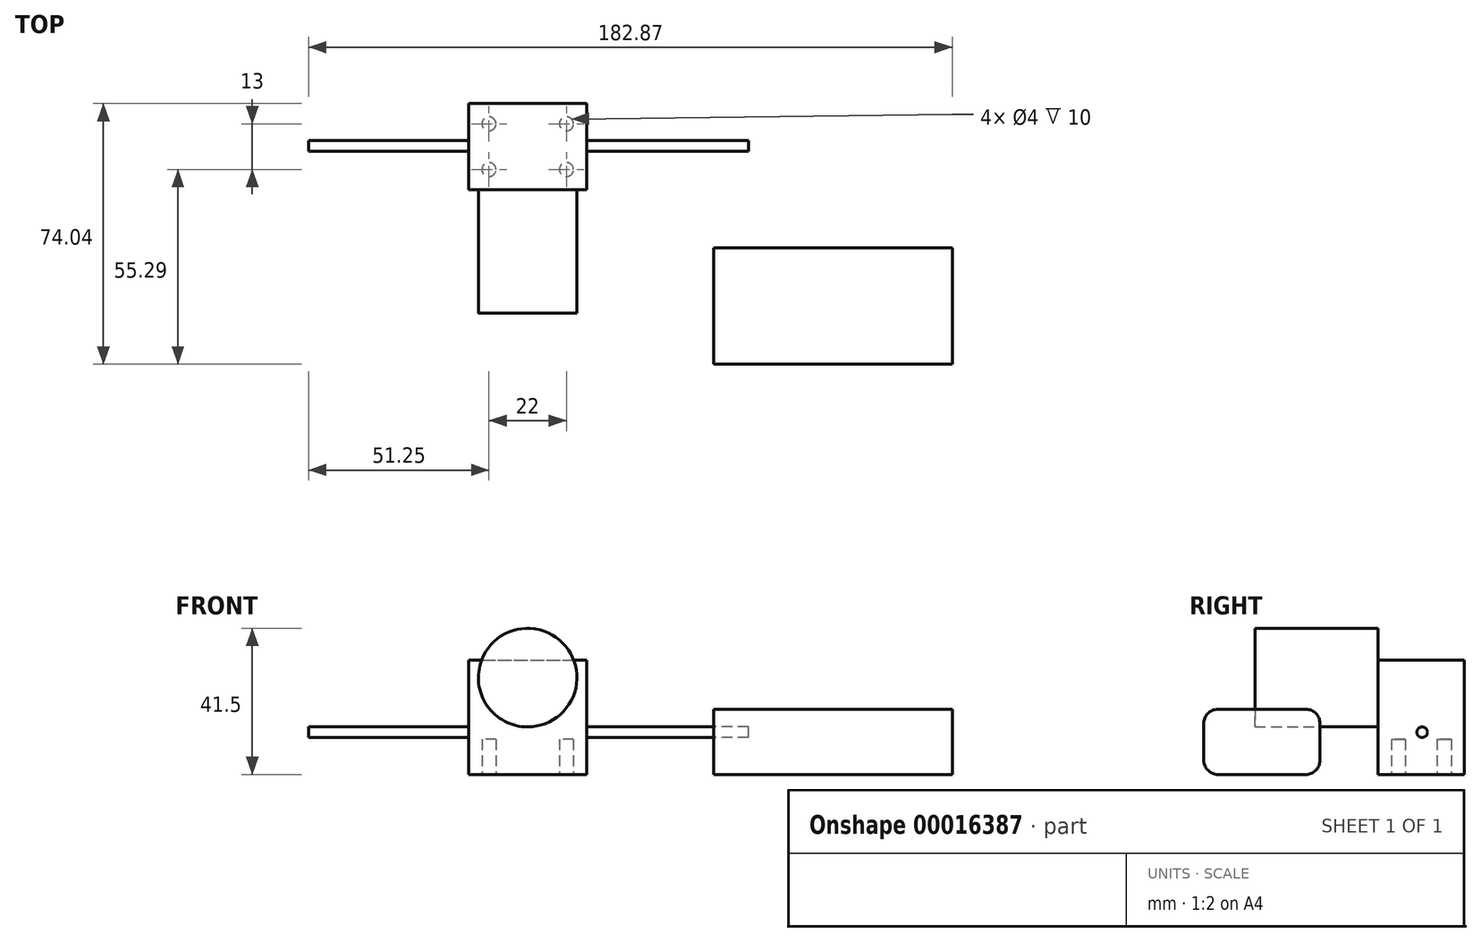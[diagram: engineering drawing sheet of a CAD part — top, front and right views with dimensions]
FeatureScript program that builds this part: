
annotation { "Feature Type Name" : "Feature", "Feature Type Description" : "" }
export const myFeature = defineFeature(function(context is Context, id is Id, definition is map)
    precondition{}
    {
        {
            var Q0;
            Q0=qCreatedBy(makeId("Top.planeOp"),FACE);
            var sketch = newSketch(context, id + "F0", { "sketchPlane" : qUnion([Q0])});
            skLineSegment(sketch, "E0.bottom", {"start": v(-16.75, 12.25) * mm, "end": v(16.75, 12.25) * mm});
            skLineSegment(sketch, "E0.top", {"start": v(-16.75, -12.25) * mm, "end": v(16.75, -12.25) * mm});
            skLineSegment(sketch, "E0.left", {"start": v(-16.75, 12.25) * mm, "end": v(-16.75, -12.25) * mm});
            skLineSegment(sketch, "E0.right", {"start": v(16.75, 12.25) * mm, "end": v(16.75, -12.25) * mm});
            skLineSegment(sketch, "E1.bottom", {"start": v(-11, 6.5) * mm, "end": v(11, 6.5) * mm, "construction": true});
            skLineSegment(sketch, "E1.top", {"start": v(-11, -6.5) * mm, "end": v(11, -6.5) * mm, "construction": true});
            skLineSegment(sketch, "E1.left", {"start": v(-11, 6.5) * mm, "end": v(-11, -6.5) * mm, "construction": true});
            skLineSegment(sketch, "E1.right", {"start": v(11, 6.5) * mm, "end": v(11, -6.5) * mm, "construction": true});
            skCircle(sketch, "E2", {"center": v(-11, 6.5) * mm, "radius": 2 * mm});
            skCircle(sketch, "E3", {"center": v(11, 6.5) * mm, "radius": 2 * mm});
            skCircle(sketch, "E4", {"center": v(11, -6.5) * mm, "radius": 2 * mm});
            skCircle(sketch, "E5", {"center": v(-11, -6.5) * mm, "radius": 2 * mm});
            skLineSegment(sketch, "E6", {"start": v(0, 0) * mm, "end": v(0, 25.06) * mm, "construction": true});
            skLineSegment(sketch, "E7", {"start": v(0, 0) * mm, "end": v(19.27, 0) * mm, "construction": true});
            skSolve(sketch);
        }
        {
            var Q0;
            Q0=makeQuery(id+"F0.imprint","IMPRINT",FACE,{"disambiguationData":[TD([[makeQuery(id+"F0.imprint","IMPRINT",EDGE,{"derivedFrom":sQuery(id+"F0.wireOp",EDGE,"E0.bottom")}),-1.0]])]});
            var Q1;
            Q1=makeQuery(id+"F0.imprint","IMPRINT",FACE,{"disambiguationData":[TD([[makeQuery(id+"F0.imprint","IMPRINT",EDGE,{"derivedFrom":sQuery(id+"F0.wireOp",EDGE,"E3")}),1.0]])]});
            var Q2;
            Q2=makeQuery(id+"F0.imprint","IMPRINT",FACE,{"disambiguationData":[TD([[makeQuery(id+"F0.imprint","IMPRINT",EDGE,{"derivedFrom":sQuery(id+"F0.wireOp",EDGE,"E2")}),1.0]])]});
            var Q3;
            Q3=makeQuery(id+"F0.imprint","IMPRINT",FACE,{"disambiguationData":[TD([[makeQuery(id+"F0.imprint","IMPRINT",EDGE,{"derivedFrom":sQuery(id+"F0.wireOp",EDGE,"E5")}),1.0]])]});
            var Q4;
            Q4=makeQuery(id+"F0.imprint","IMPRINT",FACE,{"disambiguationData":[TD([[makeQuery(id+"F0.imprint","IMPRINT",EDGE,{"derivedFrom":sQuery(id+"F0.wireOp",EDGE,"E4")}),1.0]])]});
            extrude(context, id + "F1", {"entities" : qUnion([Q0, Q1, Q2, Q3, Q4]), "depth" : 32.5 * mm});
        }
        {
            var Q0;
            Q0=makeQuery(id+"F1.opExtrude","SWEPT_FACE",FACE,{"disambiguationData":[OSD([sQuery(id+"F0.wireOp",EDGE,"E0.top")])]});
            var sketch = newSketch(context, id + "F2", { "sketchPlane" : qUnion([Q0])});
            skLineSegment(sketch, "E8", {"start": v(0, 0) * mm, "end": v(0, 55) * mm, "construction": true});
            skCircle(sketch, "E9", {"center": v(0, 27.5) * mm, "radius": 14 * mm});
            skSolve(sketch);
        }
        {
            var Q0;
            {var subQ0=makeQuery(id+"F1.opExtrude","CAP_EDGE",EDGE,{"disambiguationData":[OSD([sQuery(id+"F0.wireOp",EDGE,"E0.top")])],"isStart":false});var subQ1=sQuery(id+"F2.wireOp",EDGE,"E9");var subQ3=makeQuery(id+"F2.imprint","INTERSECT",VERTEX,{"disambiguationData":[OD(0.0)],"derivedFrom":[subQ0,subQ1]});Q0=makeQuery(id+"F2.imprint","IMPRINT",FACE,{"disambiguationData":[TD([[makeQuery(id+"F2.imprint","IMPRINT",EDGE,{"disambiguationData":[TD([[subQ3,-1.0]])],"derivedFrom":subQ1}),1.0]])]});}
            var Q1;
            {var subQ0=makeQuery(id+"F1.opExtrude","CAP_EDGE",EDGE,{"disambiguationData":[OSD([sQuery(id+"F0.wireOp",EDGE,"E0.top")])],"isStart":false});var subQ1=sQuery(id+"F2.wireOp",EDGE,"E9");var subQ3=makeQuery(id+"F2.imprint","INTERSECT",VERTEX,{"disambiguationData":[OD(0.0)],"derivedFrom":[subQ0,subQ1]});Q1=makeQuery(id+"F2.imprint","IMPRINT",FACE,{"disambiguationData":[TD([[makeQuery(id+"F2.imprint","IMPRINT",EDGE,{"disambiguationData":[TD([[subQ3,1.0]])],"derivedFrom":subQ1}),1.0]])]});}
            extrude(context, id + "F3", {"entities" : qUnion([Q0, Q1]), "operationType" : NewBodyOperationType.ADD, "depth" : 35 * mm});
        }
        {
            var Q0;
            Q0=makeQuery(id+"F0.imprint","IMPRINT",FACE,{"disambiguationData":[TD([[makeQuery(id+"F0.imprint","IMPRINT",EDGE,{"derivedFrom":sQuery(id+"F0.wireOp",EDGE,"E3")}),1.0]])]});
            var Q1;
            Q1=makeQuery(id+"F0.imprint","IMPRINT",FACE,{"disambiguationData":[TD([[makeQuery(id+"F0.imprint","IMPRINT",EDGE,{"derivedFrom":sQuery(id+"F0.wireOp",EDGE,"E2")}),1.0]])]});
            var Q2;
            Q2=makeQuery(id+"F0.imprint","IMPRINT",FACE,{"disambiguationData":[TD([[makeQuery(id+"F0.imprint","IMPRINT",EDGE,{"derivedFrom":sQuery(id+"F0.wireOp",EDGE,"E5")}),1.0]])]});
            var Q3;
            Q3=makeQuery(id+"F0.imprint","IMPRINT",FACE,{"disambiguationData":[TD([[makeQuery(id+"F0.imprint","IMPRINT",EDGE,{"derivedFrom":sQuery(id+"F0.wireOp",EDGE,"E4")}),1.0]])]});
            extrude(context, id + "F4", {"entities" : qUnion([Q0, Q1, Q2, Q3]), "operationType" : NewBodyOperationType.REMOVE, "depth" : 10 * mm});
        }
        {
            var Q0;
            Q0=makeQuery(id+"F1.opExtrude","SWEPT_FACE",FACE,{"disambiguationData":[OSD([sQuery(id+"F0.wireOp",EDGE,"E0.right")])]});
            var sketch = newSketch(context, id + "F5", { "sketchPlane" : qUnion([Q0])});
            skCircle(sketch, "E10", {"center": v(0.25, 12) * mm, "radius": 1.5 * mm});
            skSolve(sketch);
        }
        {
            var Q0;
            Q0=makeQuery(id+"F5.imprint","IMPRINT",FACE,{"disambiguationData":[TD([[makeQuery(id+"F5.imprint","IMPRINT",EDGE,{"derivedFrom":sQuery(id+"F5.wireOp",EDGE,"E10")}),1.0]])]});
            extrude(context, id + "F6", {"entities" : qUnion([Q0]), "operationType" : NewBodyOperationType.ADD, "depth" : 46 * mm, "hasSecondDirection" : true, "secondDirectionOppositeDirection" : true, "secondDirectionDepth" : 79 * mm});
        }
        {
            var Q0;
            Q0=qCreatedBy(makeId("Top.planeOp"),FACE);
            var sketch = newSketch(context, id + "F7", { "sketchPlane" : qUnion([Q0])});
            skLineSegment(sketch, "E11.bottom", {"start": v(52.82, -28.79) * mm, "end": v(120.62, -28.79) * mm});
            skLineSegment(sketch, "E11.top", {"start": v(52.82, -61.79) * mm, "end": v(120.62, -61.79) * mm});
            skLineSegment(sketch, "E11.left", {"start": v(52.82, -28.79) * mm, "end": v(52.82, -61.79) * mm});
            skLineSegment(sketch, "E11.right", {"start": v(120.62, -28.79) * mm, "end": v(120.62, -61.79) * mm});
            skSolve(sketch);
        }
        {
            var Q0;
            Q0=makeQuery(id+"F7.imprint","IMPRINT",FACE,{"disambiguationData":[TD([[makeQuery(id+"F7.imprint","IMPRINT",EDGE,{"derivedFrom":sQuery(id+"F7.wireOp",EDGE,"E11.bottom")}),-1.0]])]});
            extrude(context, id + "F8", {"entities" : qUnion([Q0]), "depth" : 18.5 * mm});
        }
        {
            var Q0;
            Q0=makeQuery(id+"F8.opExtrude","CAP_EDGE",EDGE,{"disambiguationData":[OSD([sQuery(id+"F7.wireOp",EDGE,"E11.bottom")])],"isStart":true});
            var Q1;
            Q1=makeQuery(id+"F8.opExtrude","CAP_EDGE",EDGE,{"disambiguationData":[OSD([sQuery(id+"F7.wireOp",EDGE,"E11.bottom")])],"isStart":false});
            var Q2;
            Q2=makeQuery(id+"F8.opExtrude","CAP_EDGE",EDGE,{"disambiguationData":[OSD([sQuery(id+"F7.wireOp",EDGE,"E11.top")])],"isStart":false});
            var Q3;
            Q3=makeQuery(id+"F8.opExtrude","CAP_EDGE",EDGE,{"disambiguationData":[OSD([sQuery(id+"F7.wireOp",EDGE,"E11.top")])],"isStart":true});
            fillet(context, id + "F9", {"entities" : qUnion([Q0, Q1, Q2, Q3]), "radius" : 4 * mm, "tangentPropagation" : true, "allowEdgeOverflow" : false});
        }
    });
